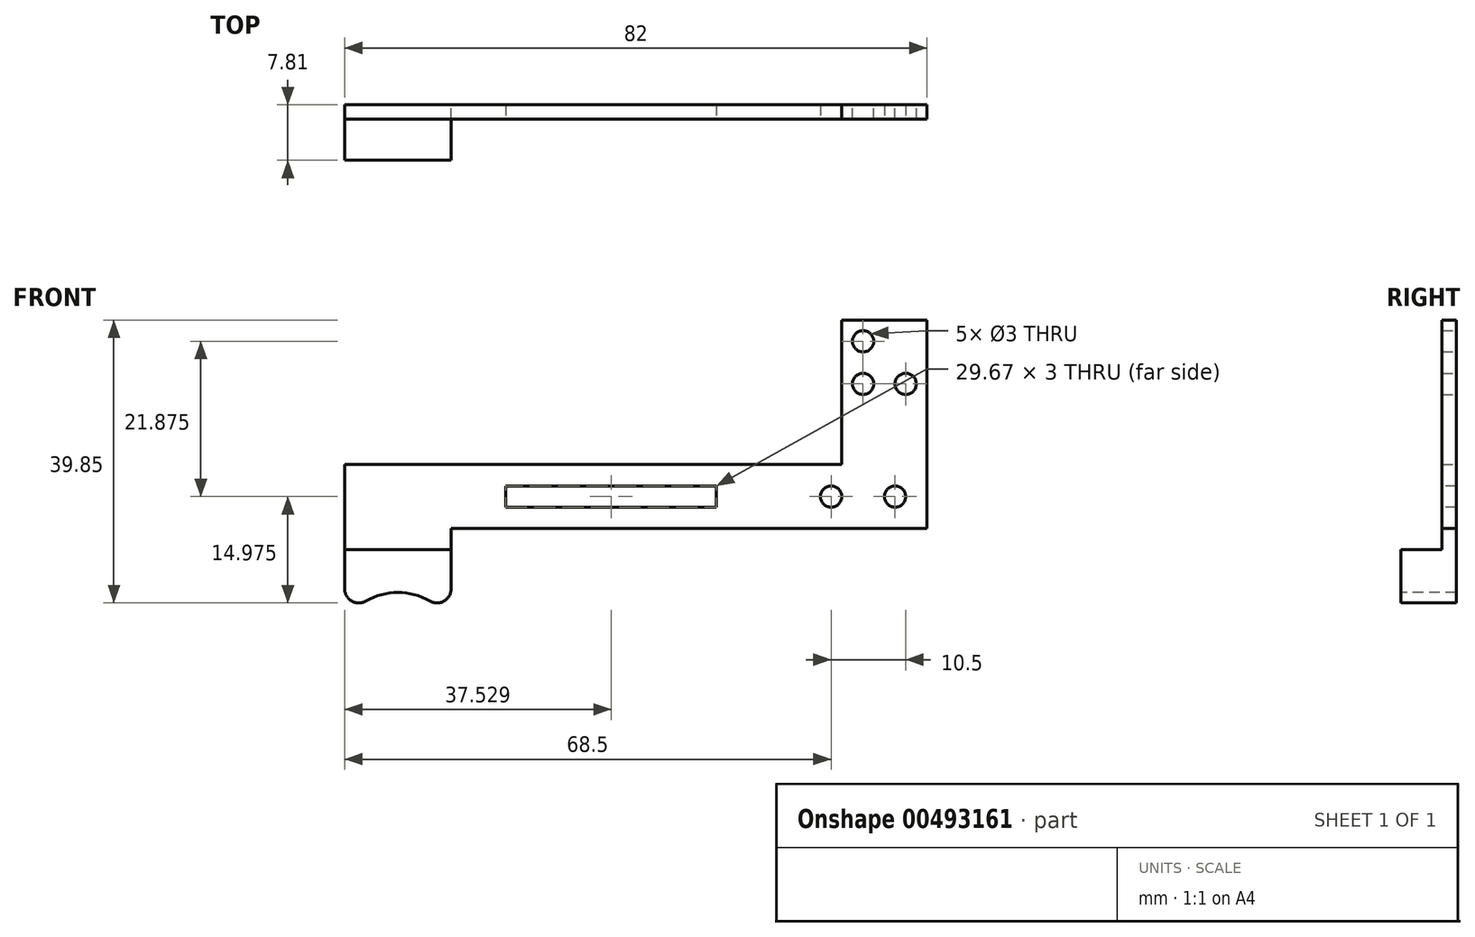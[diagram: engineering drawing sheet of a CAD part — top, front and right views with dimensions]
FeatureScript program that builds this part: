
annotation { "Feature Type Name" : "Feature", "Feature Type Description" : "" }
export const myFeature = defineFeature(function(context is Context, id is Id, definition is map)
    precondition{}
    {
        {
            var Q0;
            Q0=qCreatedBy(makeId("Front.planeOp"),FACE);
            var sketch = newSketch(context, id + "F0", { "sketchPlane" : qUnion([Q0])});
            skCircle(sketch, "E0", {"center": v(0, 0) * mm, "radius": 1.5 * mm});
            skCircle(sketch, "E1", {"center": v(0, -6) * mm, "radius": 1.5 * mm});
            skCircle(sketch, "E2", {"center": v(6, -6) * mm, "radius": 1.5 * mm});
            skLineSegment(sketch, "E3.bottom", {"start": v(-3, 3) * mm, "end": v(9, 3) * mm});
            skLineSegment(sketch, "E3.top", {"start": v(-3, -13.5) * mm, "end": v(9, -13.5) * mm});
            skLineSegment(sketch, "E3.left", {"start": v(-3, 3) * mm, "end": v(-3, -13.5) * mm});
            skLineSegment(sketch, "E3.right", {"start": v(9, 3) * mm, "end": v(9, -13.5) * mm});
            skLineSegment(sketch, "E4.bottom", {"start": v(9, -13.5) * mm, "end": v(-3, -13.5) * mm});
            skLineSegment(sketch, "E4.top", {"start": v(9, -26.38) * mm, "end": v(-3, -26.38) * mm});
            skLineSegment(sketch, "E4.left", {"start": v(9, -13.5) * mm, "end": v(9, -26.38) * mm});
            skLineSegment(sketch, "E4.right", {"start": v(-3, -13.5) * mm, "end": v(-3, -26.38) * mm});
            skLineSegment(sketch, "E5.bottom", {"start": v(-3, -17.38) * mm, "end": v(-73, -17.38) * mm});
            skLineSegment(sketch, "E5.top", {"start": v(-3, -26.38) * mm, "end": v(-73, -26.38) * mm});
            skLineSegment(sketch, "E5.left", {"start": v(-3, -17.38) * mm, "end": v(-3, -26.38) * mm});
            skLineSegment(sketch, "E5.right", {"start": v(-73, -17.38) * mm, "end": v(-73, -26.38) * mm});
            skLineSegment(sketch, "E6.bottom", {"start": v(-73, -26.38) * mm, "end": v(-58, -26.38) * mm});
            skLineSegment(sketch, "E6.top", {"start": v(-73, -29.38) * mm, "end": v(-58, -29.38) * mm});
            skLineSegment(sketch, "E6.left", {"start": v(-73, -26.38) * mm, "end": v(-73, -29.38) * mm});
            skLineSegment(sketch, "E6.right", {"start": v(-58, -26.38) * mm, "end": v(-58, -29.38) * mm});
            skSolve(sketch);
        }
        {
            var Q0;
            Q0 = qSketchRegion(id + "F0", true);
            extrude(context, id + "F1", {"entities" : qUnion([Q0]), "depth" : 2 * mm});
        }
        {
            var Q0;
            Q0=makeQuery(id+"F1.opExtrude","SWEPT_FACE",FACE,{"disambiguationData":[OSD([sQuery(id+"F0.wireOp",EDGE,"E6.top")])]});
            var sketch = newSketch(context, id + "F2", { "sketchPlane" : qUnion([Q0])});
            skLineSegment(sketch, "E7.bottom", {"start": v(-73, 0) * mm, "end": v(-58, 0) * mm});
            skLineSegment(sketch, "E7.top", {"start": v(-73, 7.8) * mm, "end": v(-58, 7.8) * mm});
            skLineSegment(sketch, "E7.left", {"start": v(-73, 0) * mm, "end": v(-73, 7.8) * mm});
            skLineSegment(sketch, "E7.right", {"start": v(-58, 0) * mm, "end": v(-58, 7.8) * mm});
            skSolve(sketch);
        }
        {
            var Q0;
            Q0 = qSketchRegion(id + "F2", true);
            extrude(context, id + "F3", {"entities" : qUnion([Q0]), "operationType" : NewBodyOperationType.ADD, "depth" : 10 * mm});
        }
        {
            var Q0;
            Q0=makeQuery(id+"F3.opExtrude","SWEPT_FACE",FACE,{"disambiguationData":[OSD([sQuery(id+"F2.wireOp",EDGE,"E7.top")])]});
            var sketch = newSketch(context, id + "F4", { "sketchPlane" : qUnion([Q0])});
            skArc(sketch, "E8", {"start": v(-58, -39.38) * mm, "mid": v(-65.5, -35.39) * mm, "end": v(-73, -39.38) * mm});
            skLineSegment(sketch, "E9", {"start": v(-73, -39.38) * mm, "end": v(-58, -39.38) * mm});
            skSolve(sketch);
        }
        {
            var Q0;
            Q0 = qSketchRegion(id + "F4", true);
            extrude(context, id + "F5", {"entities" : qUnion([Q0]), "operationType" : NewBodyOperationType.REMOVE, "oppositeDirection" : true, "depth" : 25 * mm});
        }
        {
            var Q0;
            {var subQ0=sQuery(id+"F2.wireOp",EDGE,"E7.left");Q0=makeQuery(id+"F5.boolean.opBoolean","MERGE",EDGE,{"derivedFrom":[makeQuery(id+"F3.opExtrude","CAP_EDGE",EDGE,{"disambiguationData":[OSD([subQ0])],"isStart":false}),makeQuery(id+"F5.opExtrude","SWEPT_EDGE",EDGE,{"disambiguationData":[OSD([sQuery(id+"F2.wireOp",EDGE,"E7.top"),subQ0,sQuery(id+"F4.wireOp",EDGE,"E8"),sQuery(id+"F4.wireOp",EDGE,"E9")])]})]});}
            var Q1;
            {var subQ0=sQuery(id+"F2.wireOp",EDGE,"E7.right");Q1=makeQuery(id+"F5.boolean.opBoolean","MERGE",EDGE,{"derivedFrom":[makeQuery(id+"F3.opExtrude","CAP_EDGE",EDGE,{"disambiguationData":[OSD([subQ0])],"isStart":false}),makeQuery(id+"F5.opExtrude","SWEPT_EDGE",EDGE,{"disambiguationData":[OSD([sQuery(id+"F2.wireOp",EDGE,"E7.top"),subQ0,sQuery(id+"F4.wireOp",EDGE,"E8"),sQuery(id+"F4.wireOp",EDGE,"E9")])]})]});}
            fillet(context, id + "F6", {"entities" : qUnion([Q0, Q1]), "radius" : 2 * mm, "tangentPropagation" : true, "allowEdgeOverflow" : false});
        }
        {
            var Q0;
            Q0=makeQuery(id+"F1.opExtrude","CAP_FACE",FACE,{"disambiguationData":[OSD([sQuery(id+"F0.wireOp",EDGE,"E0"),sQuery(id+"F0.wireOp",EDGE,"E1"),sQuery(id+"F0.wireOp",EDGE,"E2"),sQuery(id+"F0.wireOp",EDGE,"E3.bottom"),sQuery(id+"F0.wireOp",EDGE,"E3.left"),sQuery(id+"F0.wireOp",EDGE,"E3.right"),sQuery(id+"F0.wireOp",EDGE,"E4.top"),sQuery(id+"F0.wireOp",EDGE,"E4.left"),sQuery(id+"F0.wireOp",EDGE,"E4.right"),sQuery(id+"F0.wireOp",EDGE,"E5.bottom"),sQuery(id+"F0.wireOp",EDGE,"E5.top"),sQuery(id+"F0.wireOp",EDGE,"E5.right"),sQuery(id+"F0.wireOp",EDGE,"E6.top"),sQuery(id+"F0.wireOp",EDGE,"E6.left"),sQuery(id+"F0.wireOp",EDGE,"E6.right")])],"isStart":false});
            var sketch = newSketch(context, id + "F7", { "sketchPlane" : qUnion([Q0])});
            skLineSegment(sketch, "E10.bottom", {"start": v(-50.3, -23.38) * mm, "end": v(-20.64, -23.38) * mm});
            skLineSegment(sketch, "E10.top", {"start": v(-50.3, -20.38) * mm, "end": v(-20.64, -20.38) * mm});
            skLineSegment(sketch, "E10.left", {"start": v(-50.3, -23.38) * mm, "end": v(-50.3, -20.38) * mm});
            skLineSegment(sketch, "E10.right", {"start": v(-20.64, -23.38) * mm, "end": v(-20.64, -20.38) * mm});
            skSolve(sketch);
        }
        {
            var Q0;
            Q0 = qSketchRegion(id + "F7", true);
            extrude(context, id + "F8", {"entities" : qUnion([Q0]), "operationType" : NewBodyOperationType.REMOVE, "oppositeDirection" : true, "depth" : 25 * mm});
        }
        {
            var Q0;
            Q0=makeQuery(id+"F1.opExtrude","CAP_FACE",FACE,{"disambiguationData":[OSD([sQuery(id+"F0.wireOp",EDGE,"E0"),sQuery(id+"F0.wireOp",EDGE,"E1"),sQuery(id+"F0.wireOp",EDGE,"E2"),sQuery(id+"F0.wireOp",EDGE,"E3.bottom"),sQuery(id+"F0.wireOp",EDGE,"E3.left"),sQuery(id+"F0.wireOp",EDGE,"E3.right"),sQuery(id+"F0.wireOp",EDGE,"E4.top"),sQuery(id+"F0.wireOp",EDGE,"E4.left"),sQuery(id+"F0.wireOp",EDGE,"E4.right"),sQuery(id+"F0.wireOp",EDGE,"E5.bottom"),sQuery(id+"F0.wireOp",EDGE,"E5.top"),sQuery(id+"F0.wireOp",EDGE,"E5.right"),sQuery(id+"F0.wireOp",EDGE,"E6.top"),sQuery(id+"F0.wireOp",EDGE,"E6.left"),sQuery(id+"F0.wireOp",EDGE,"E6.right")])],"isStart":false});
            var sketch = newSketch(context, id + "F9", { "sketchPlane" : qUnion([Q0])});
            skCircle(sketch, "E11", {"center": v(-4.5, -21.88) * mm, "radius": 1.5 * mm});
            skCircle(sketch, "E12", {"center": v(4.5, -21.88) * mm, "radius": 1.5 * mm});
            skSolve(sketch);
        }
        {
            var Q0;
            Q0 = qSketchRegion(id + "F9", true);
            extrude(context, id + "F10", {"entities" : qUnion([Q0]), "operationType" : NewBodyOperationType.REMOVE, "oppositeDirection" : true, "depth" : 25 * mm});
        }
    });
